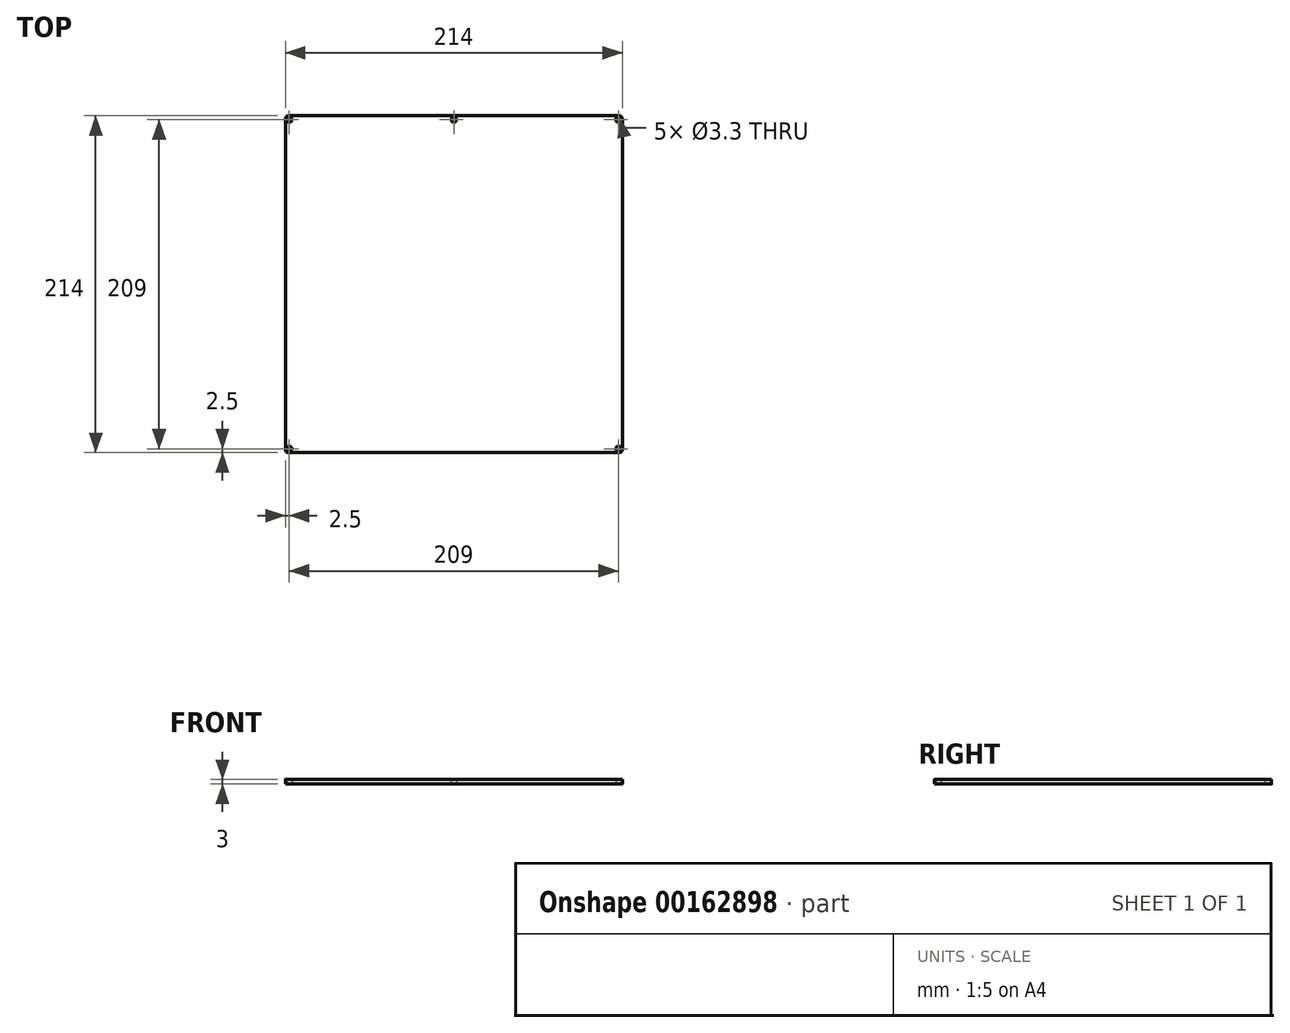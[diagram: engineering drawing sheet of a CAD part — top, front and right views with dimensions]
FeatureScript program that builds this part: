
annotation { "Feature Type Name" : "Feature", "Feature Type Description" : "" }
export const myFeature = defineFeature(function(context is Context, id is Id, definition is map)
    precondition{}
    {
        {
            var Q0;
            Q0=qCreatedBy(makeId("Top.planeOp"),FACE);
            var sketch = newSketch(context, id + "F0", { "sketchPlane" : qUnion([Q0])});
            skLineSegment(sketch, "E0.bottom", {"start": v(107, -107) * mm, "end": v(-107, -107) * mm});
            skLineSegment(sketch, "E0.top", {"start": v(107, 107) * mm, "end": v(-107, 107) * mm});
            skLineSegment(sketch, "E0.left", {"start": v(107, -107) * mm, "end": v(107, 107) * mm});
            skLineSegment(sketch, "E0.right", {"start": v(-107, -107) * mm, "end": v(-107, 107) * mm});
            skPoint(sketch, "E0.middle", {"position": v(0, 0) * mm});
            skLineSegment(sketch, "E1.bottom", {"start": v(104.5, -104.5) * mm, "end": v(-104.5, -104.5) * mm, "construction": true});
            skLineSegment(sketch, "E1.top", {"start": v(104.5, 104.5) * mm, "end": v(-104.5, 104.5) * mm, "construction": true});
            skLineSegment(sketch, "E1.left", {"start": v(104.5, -104.5) * mm, "end": v(104.5, 104.5) * mm, "construction": true});
            skLineSegment(sketch, "E1.right", {"start": v(-104.5, -104.5) * mm, "end": v(-104.5, 104.5) * mm, "construction": true});
            skPoint(sketch, "E2", {"position": v(-104.5, 104.5) * mm});
            skPoint(sketch, "E3", {"position": v(104.5, 104.5) * mm});
            skPoint(sketch, "E4", {"position": v(104.5, -104.5) * mm});
            skPoint(sketch, "E5", {"position": v(-104.5, -104.5) * mm});
            skPoint(sketch, "E6", {"position": v(0, 104.5) * mm});
            skSolve(sketch);
        }
        {
            var Q0;
            Q0=makeQuery(id+"F0.imprint","IMPRINT",FACE,{"disambiguationData":[TD([[makeQuery(id+"F0.imprint","IMPRINT",EDGE,{"derivedFrom":sQuery(id+"F0.wireOp",EDGE,"E0.bottom")}),-1.0]])]});
            extrude(context, id + "F1", {"entities" : qUnion([Q0]), "depth" : 3 * mm});
        }
        {
            var Q0;
            Q0=sQuery(id+"F0.wireOp",VERTEX,"E4");
            var Q1;
            Q1=sQuery(id+"F0.wireOp",VERTEX,"E5");
            var Q2;
            Q2=sQuery(id+"F0.wireOp",VERTEX,"E2");
            var Q3;
            Q3=sQuery(id+"F0.wireOp",VERTEX,"E6");
            var Q4;
            Q4=sQuery(id+"F0.wireOp",VERTEX,"E3");
            var Q5;
            Q5=makeQuery(id+"F1.opExtrude","SWEPT_BODY",BODY,{"disambiguationData":[OSD([sQuery(id+"F0.wireOp",EDGE,"E0.bottom"),sQuery(id+"F0.wireOp",EDGE,"E0.top"),sQuery(id+"F0.wireOp",EDGE,"E0.left"),sQuery(id+"F0.wireOp",EDGE,"E0.right")])]});
            hole(context, id + "F2", {"style" : HoleStyle.SIMPLE, "endStyle" : HoleEndStyle.THROUGH, "oppositeDirection" : true, "standardTappedOrClearance" : lookupTablePath({ "standard" : "ISO", "fit" : "Normal", "size" : "M3", "type" : "Clearance" }), "standardBlindInLast" : lookupTablePath({ "fit" : "Standard", "standard" : "ISO", "size" : "M3", "type" : "Clearance" }), "holeDiameter" : 3.3 * mm, "startFromSketch" : true, "locations" : qUnion([Q0, Q1, Q2, Q3, Q4]), "scope" : qUnion([Q5]), "isTappedThrough" : true});
        }
        {
            var Q0;
            Q0=makeQuery(id+"F1.opExtrude","SWEPT_EDGE",EDGE,{"disambiguationData":[OSD([sQuery(id+"F0.wireOp",EDGE,"E0.bottom"),sQuery(id+"F0.wireOp",EDGE,"E0.right")])]});
            var Q1;
            Q1=makeQuery(id+"F1.opExtrude","SWEPT_EDGE",EDGE,{"disambiguationData":[OSD([sQuery(id+"F0.wireOp",EDGE,"E0.bottom"),sQuery(id+"F0.wireOp",EDGE,"E0.left")])]});
            var Q2;
            Q2=makeQuery(id+"F1.opExtrude","SWEPT_EDGE",EDGE,{"disambiguationData":[OSD([sQuery(id+"F0.wireOp",EDGE,"E0.top"),sQuery(id+"F0.wireOp",EDGE,"E0.left")])]});
            var Q3;
            Q3=makeQuery(id+"F1.opExtrude","SWEPT_EDGE",EDGE,{"disambiguationData":[OSD([sQuery(id+"F0.wireOp",EDGE,"E0.top"),sQuery(id+"F0.wireOp",EDGE,"E0.right")])]});
            fillet(context, id + "F3", {"entities" : qUnion([Q0, Q1, Q2, Q3]), "radius" : 2 * mm, "tangentPropagation" : true, "allowEdgeOverflow" : false});
        }
    });
